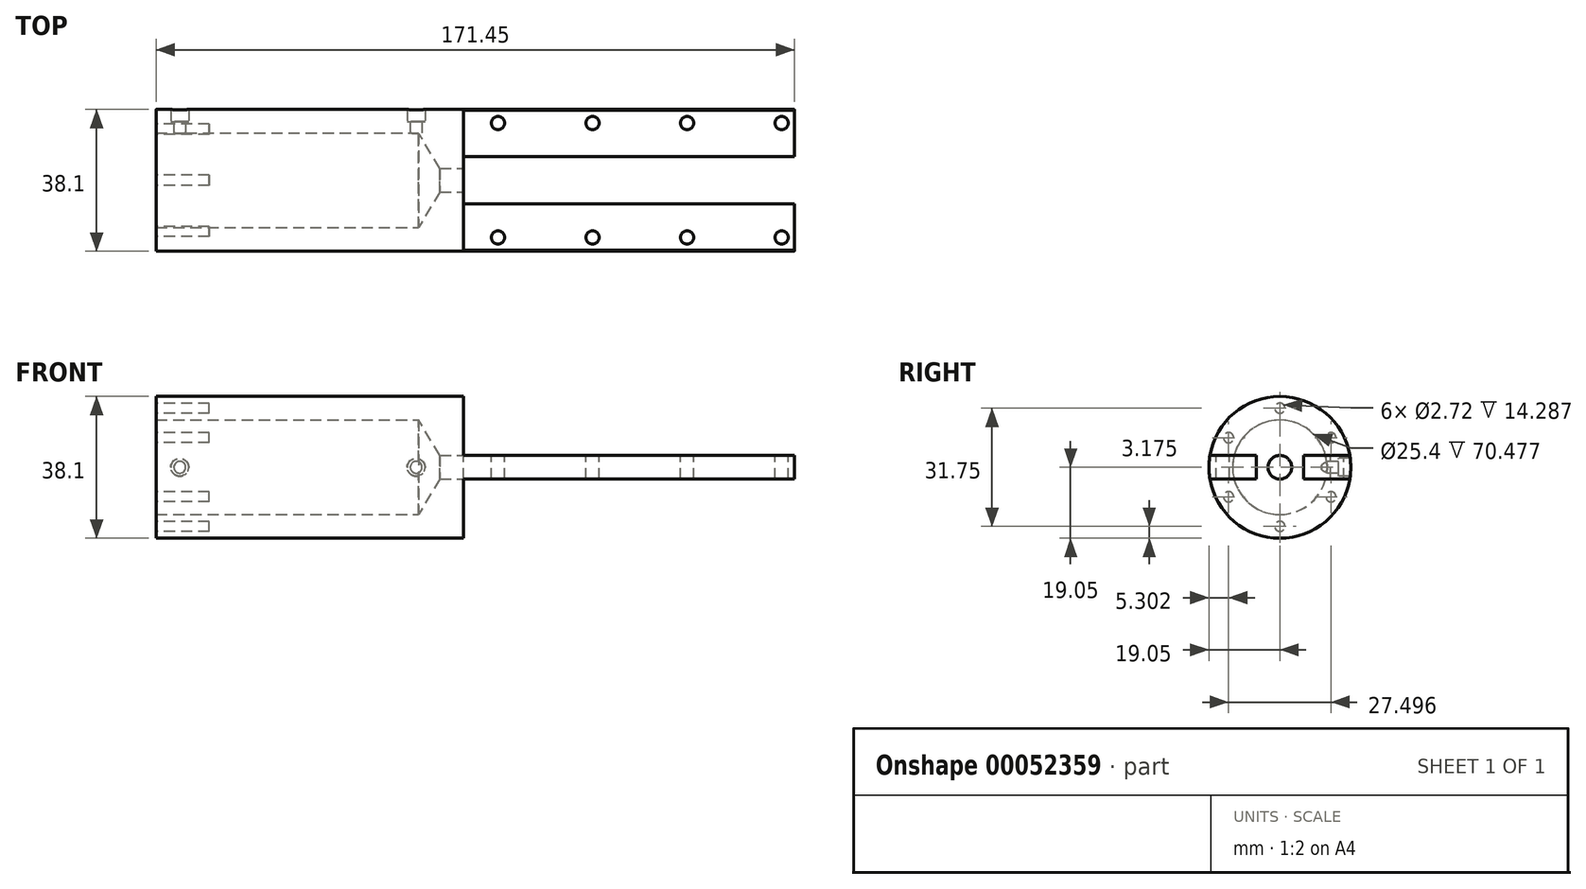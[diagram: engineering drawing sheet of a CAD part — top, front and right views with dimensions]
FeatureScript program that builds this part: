
annotation { "Feature Type Name" : "Feature", "Feature Type Description" : "" }
export const myFeature = defineFeature(function(context is Context, id is Id, definition is map)
    precondition{}
    {
        {
            var Q0;
            Q0=qCreatedBy(makeId("Right.planeOp"),FACE);
            var sketch = newSketch(context, id + "F0", { "sketchPlane" : qUnion([Q0])});
            skCircle(sketch, "E0", {"center": v(0, 0) * mm, "radius": 19.05 * mm});
            skSolve(sketch);
        }
        {
            var Q0;
            Q0 = qSketchRegion(id + "F0", true);
            extrude(context, id + "F1", {"entities" : qUnion([Q0]), "depth" : 171.45 * mm});
        }
        {
            var Q0;
            Q0=qCreatedBy(makeId("Front.planeOp"),FACE);
            var sketch = newSketch(context, id + "F2", { "sketchPlane" : qUnion([Q0])});
            skLineSegment(sketch, "E1.bottom", {"start": v(82.55, 3.18) * mm, "end": v(171.45, 3.18) * mm});
            skLineSegment(sketch, "E1.top", {"start": v(82.55, 19.05) * mm, "end": v(171.45, 19.05) * mm});
            skLineSegment(sketch, "E1.left", {"start": v(82.55, 3.18) * mm, "end": v(82.55, 19.05) * mm});
            skLineSegment(sketch, "E1.right", {"start": v(171.45, 3.18) * mm, "end": v(171.45, 19.05) * mm});
            skLineSegment(sketch, "E2.bottom", {"start": v(82.55, -3.18) * mm, "end": v(171.45, -3.18) * mm});
            skLineSegment(sketch, "E2.top", {"start": v(82.55, -19.05) * mm, "end": v(171.45, -19.05) * mm});
            skLineSegment(sketch, "E2.left", {"start": v(82.55, -3.18) * mm, "end": v(82.55, -19.05) * mm});
            skLineSegment(sketch, "E2.right", {"start": v(171.45, -3.18) * mm, "end": v(171.45, -19.05) * mm});
            skLineSegment(sketch, "E3", {"start": v(0, 19.05) * mm, "end": v(171.45, 19.05) * mm, "construction": true});
            skLineSegment(sketch, "E4", {"start": v(171.45, -19.05) * mm, "end": v(0, -19.05) * mm, "construction": true});
            skSolve(sketch);
        }
        {
            var Q0;
            Q0 = qSketchRegion(id + "F2", true);
            extrude(context, id + "F3", {"entities" : qUnion([Q0]), "operationType" : NewBodyOperationType.REMOVE, "oppositeDirection" : true, "depth" : 50.8 * mm, "symmetric" : true});
        }
        {
            var Q0;
            Q0=qCreatedBy(makeId("Top.planeOp"),FACE);
            var sketch = newSketch(context, id + "F4", { "sketchPlane" : qUnion([Q0])});
            skLineSegment(sketch, "E5.bottom", {"start": v(171.45, 6.35) * mm, "end": v(82.55, 6.35) * mm});
            skLineSegment(sketch, "E5.top", {"start": v(171.45, -6.35) * mm, "end": v(82.55, -6.35) * mm});
            skLineSegment(sketch, "E5.left", {"start": v(171.45, 6.35) * mm, "end": v(171.45, -6.35) * mm});
            skLineSegment(sketch, "E5.right", {"start": v(82.55, 6.35) * mm, "end": v(82.55, -6.35) * mm});
            skCircle(sketch, "E6", {"center": v(91.82, 15.37) * mm, "radius": 1.78 * mm});
            skCircle(sketch, "E7", {"center": v(91.82, -15.37) * mm, "radius": 1.78 * mm});
            skCircle(sketch, "E8.1.0.0", {"center": v(117.22, 15.37) * mm, "radius": 1.78 * mm});
            skCircle(sketch, "E8.1.0.1", {"center": v(117.22, -15.37) * mm, "radius": 1.78 * mm});
            skCircle(sketch, "E8.2.0.0", {"center": v(142.62, 15.37) * mm, "radius": 1.78 * mm});
            skCircle(sketch, "E8.2.0.1", {"center": v(142.62, -15.37) * mm, "radius": 1.78 * mm});
            skCircle(sketch, "E8.3.0.0", {"center": v(168.02, 15.37) * mm, "radius": 1.78 * mm});
            skCircle(sketch, "E8.3.0.1", {"center": v(168.02, -15.37) * mm, "radius": 1.78 * mm});
            skLineSegment(sketch, "E8.direction1", {"start": v(91.82, 15.37) * mm, "end": v(117.22, 15.37) * mm, "construction": true});
            skSolve(sketch);
        }
        {
            var Q0;
            Q0 = qSketchRegion(id + "F4", true);
            extrude(context, id + "F5", {"entities" : qUnion([Q0]), "operationType" : NewBodyOperationType.REMOVE, "oppositeDirection" : true, "depth" : 50.8 * mm, "symmetric" : true});
        }
        {
            var Q0;
            Q0=qCreatedBy(makeId("Top.planeOp"),FACE);
            var sketch = newSketch(context, id + "F6", { "sketchPlane" : qUnion([Q0])});
            skLineSegment(sketch, "E9", {"start": v(0, 0) * mm, "end": v(82.55, 0) * mm});
            skLineSegment(sketch, "E10", {"start": v(82.55, 0) * mm, "end": v(82.55, 3.18) * mm});
            skLineSegment(sketch, "E11", {"start": v(82.55, 3.18) * mm, "end": v(76.2, 3.18) * mm});
            skLineSegment(sketch, "E12", {"start": v(76.2, 3.18) * mm, "end": v(70.48, 12.7) * mm});
            skLineSegment(sketch, "E13", {"start": v(70.48, 12.7) * mm, "end": v(0, 12.7) * mm});
            skLineSegment(sketch, "E14", {"start": v(0, 12.7) * mm, "end": v(0, 0) * mm});
            skSolve(sketch);
        }
        {
            var Q0;
            Q0 = qSketchRegion(id + "F6", true);
            var Q1;
            Q1=sQuery(id+"F6.wireOp",EDGE,"E9");
            revolve(context, id + "F7", {"operationType" : NewBodyOperationType.REMOVE, "entities" : qUnion([Q0]), "axis" : qUnion([Q1]), "revolveType" : RevolveType.FULL, "oppositeDirection" : true});
        }
        {
            var Q0;
            Q0=qCreatedBy(makeId("Front.planeOp"),FACE);
            cPlane(context, id + "F8", {"entities" : qUnion([Q0]), "cplaneType" : CPlaneType.OFFSET, "offset" : 19.05 * mm, "oppositeDirection" : true, "width" : 152.4 * mm, "height" : 152.4 * mm});
        }
        {
            var Q0;
            Q0=qCreatedBy(id+"F8.planeOp",FACE);
            var sketch = newSketch(context, id + "F9", { "sketchPlane" : qUnion([Q0])});
            skPoint(sketch, "E15", {"position": v(6.35, 0) * mm});
            skPoint(sketch, "E16", {"position": v(69.85, 0) * mm});
            skSolve(sketch);
        }
        {
            var Q0;
            Q0=sQuery(id+"F9.wireOp",VERTEX,"E15");
            var Q1;
            Q1=sQuery(id+"F9.wireOp",VERTEX,"E16");
            var Q2;
            Q2=makeQuery(id+"F1.opExtrude","SWEPT_BODY",BODY,{"disambiguationData":[OSD([sQuery(id+"F0.wireOp",EDGE,"E0")])]});
            hole(context, id + "F10", {"style" : HoleStyle.C_BORE, "holeDiameter" : 3.17 * mm, "cBoreDiameter" : 4.78 * mm, "cBoreDepth" : 3.17 * mm, "endStyle" : HoleEndStyle.BLIND, "oppositeDirection" : true, "holeDepth" : 7.62 * mm, "locations" : qUnion([Q0, Q1]), "scope" : qUnion([Q2])});
        }
        {
            var Q0;
            Q0=qCreatedBy(makeId("Right.planeOp"),FACE);
            var sketch = newSketch(context, id + "F11", { "sketchPlane" : qUnion([Q0])});
            skCircle(sketch, "E17", {"center": v(0, 0) * mm, "radius": 15.88 * mm, "construction": true});
            skCircle(sketch, "E18", {"center": v(0, 15.88) * mm, "radius": 1.36 * mm});
            skCircle(sketch, "E19.1.0", {"center": v(-13.75, 7.94) * mm, "radius": 1.36 * mm});
            skCircle(sketch, "E19.2.0", {"center": v(-13.75, -7.94) * mm, "radius": 1.36 * mm});
            skCircle(sketch, "E19.3.0", {"center": v(0, -15.88) * mm, "radius": 1.36 * mm});
            skCircle(sketch, "E19.4.0", {"center": v(13.75, -7.94) * mm, "radius": 1.36 * mm});
            skCircle(sketch, "E19.5.0", {"center": v(13.75, 7.94) * mm, "radius": 1.36 * mm});
            skLineSegment(sketch, "E20", {"start": v(0, 0) * mm, "end": v(0, 15.88) * mm, "construction": true});
            skSolve(sketch);
        }
        {
            var Q0;
            Q0 = qSketchRegion(id + "F11", true);
            extrude(context, id + "F12", {"entities" : qUnion([Q0]), "operationType" : NewBodyOperationType.REMOVE, "depth" : 14.29 * mm});
        }
    });
